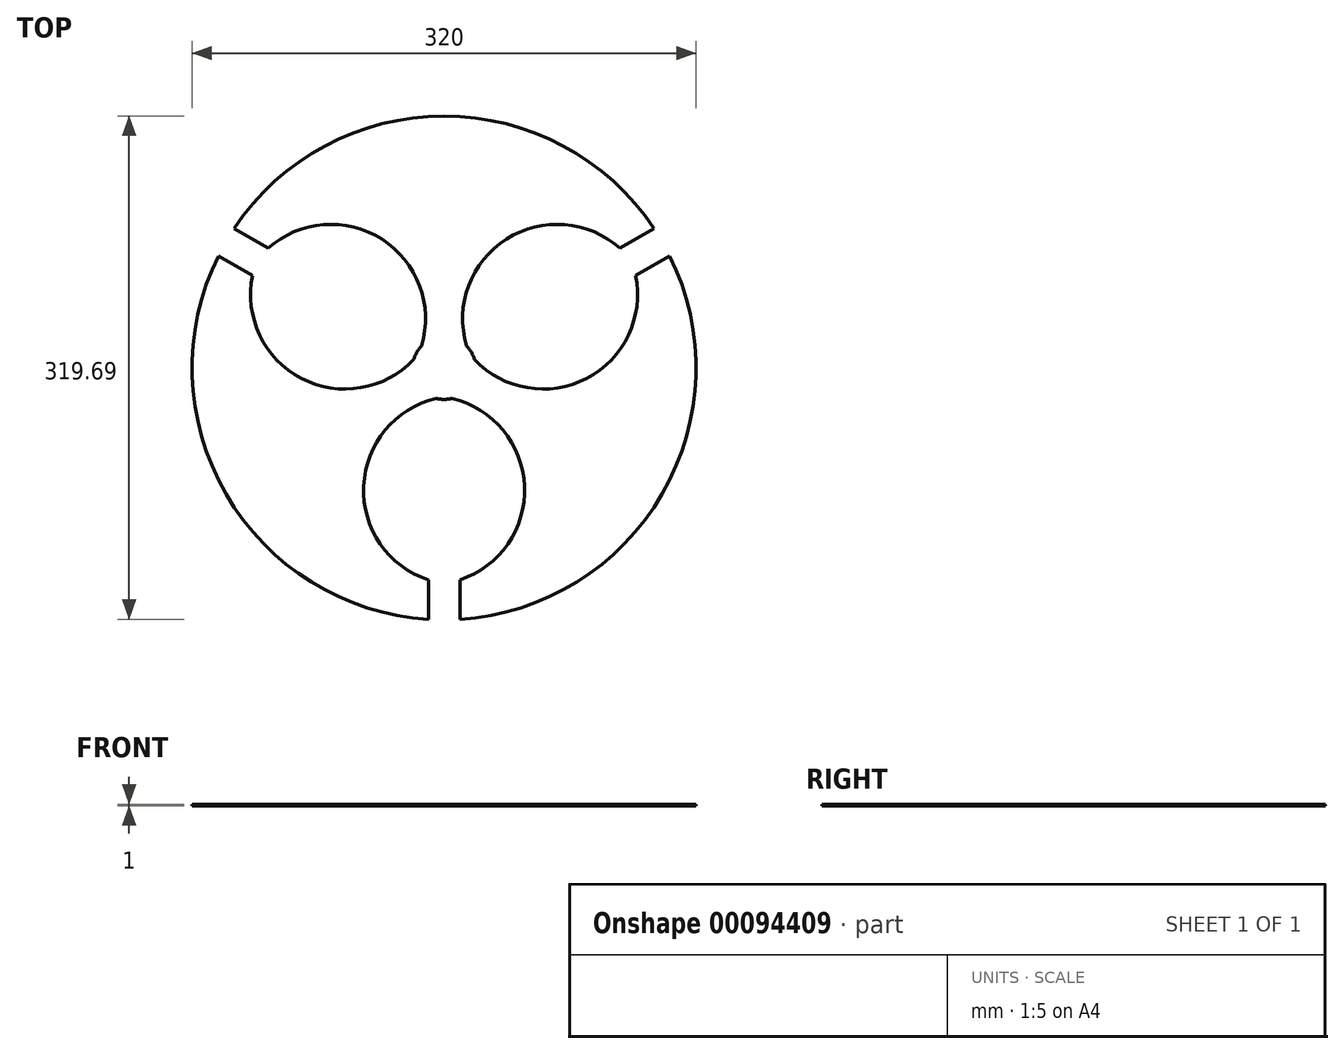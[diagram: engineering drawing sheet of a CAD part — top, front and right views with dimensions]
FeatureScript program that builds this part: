
annotation { "Feature Type Name" : "Feature", "Feature Type Description" : "" }
export const myFeature = defineFeature(function(context is Context, id is Id, definition is map)
    precondition{}
    {
        {
            var Q0;
            Q0=qCreatedBy(makeId("Top.planeOp"),FACE);
            var sketch = newSketch(context, id + "F0", { "sketchPlane" : qUnion([Q0])});
            skArc(sketch, "E0", {"start": v(-5, -19.36) * mm, "mid": v(0, -20) * mm, "end": v(5, -19.36) * mm});
            skArc(sketch, "E1", {"start": v(10, -159.69) * mm, "mid": v(138.56, -80) * mm, "end": v(143.3, 71.18) * mm});
            skLineSegment(sketch, "E2", {"start": v(0, 0) * mm, "end": v(0, -160) * mm, "construction": true});
            skLineSegment(sketch, "E3", {"start": v(0, 0) * mm, "end": v(-138.56, 80) * mm, "construction": true});
            skLineSegment(sketch, "E4", {"start": v(0, 0) * mm, "end": v(138.56, 80) * mm, "construction": true});
            skLineSegment(sketch, "E5", {"start": v(-10, -159.69) * mm, "end": v(-10, -134.69) * mm});
            skLineSegment(sketch, "E6", {"start": v(10, -159.69) * mm, "end": v(10, -134.69) * mm});
            skArc(sketch, "E7", {"start": v(-5, -19.36) * mm, "mid": v(-51.06, -75.14) * mm, "end": v(-10, -134.69) * mm});
            skArc(sketch, "E8", {"start": v(10, -134.69) * mm, "mid": v(51.06, -75.14) * mm, "end": v(5, -19.36) * mm});
            skArc(sketch, "E9.1.0", {"start": v(19.27, 5.35) * mm, "mid": v(90.6, -6.65) * mm, "end": v(121.64, 58.68) * mm});
            skLineSegment(sketch, "E9.1.1", {"start": v(133.3, 88.5) * mm, "end": v(111.64, 76) * mm});
            skLineSegment(sketch, "E9.1.2", {"start": v(143.3, 71.18) * mm, "end": v(121.64, 58.68) * mm});
            skArc(sketch, "E9.1.3", {"start": v(111.64, 76) * mm, "mid": v(39.54, 81.79) * mm, "end": v(14.27, 14.01) * mm});
            skArc(sketch, "E9.2.0", {"start": v(-14.27, 14.01) * mm, "mid": v(-39.54, 81.79) * mm, "end": v(-111.64, 76) * mm});
            skLineSegment(sketch, "E9.2.1", {"start": v(-143.3, 71.18) * mm, "end": v(-121.64, 58.68) * mm});
            skLineSegment(sketch, "E9.2.2", {"start": v(-133.3, 88.5) * mm, "end": v(-111.64, 76) * mm});
            skArc(sketch, "E9.2.3", {"start": v(-121.64, 58.68) * mm, "mid": v(-90.6, -6.65) * mm, "end": v(-19.27, 5.35) * mm});
            skArc(sketch, "E10.trimOffspring", {"start": v(-143.3, 71.18) * mm, "mid": v(-138.56, -80) * mm, "end": v(-10, -159.69) * mm});
            skArc(sketch, "E11.trimOffspring", {"start": v(133.3, 88.5) * mm, "mid": v(0, 160) * mm, "end": v(-133.3, 88.5) * mm});
            skArc(sketch, "E12.trimOffspring", {"start": v(-14.27, 14.01) * mm, "mid": v(-17.32, 10) * mm, "end": v(-19.27, 5.35) * mm});
            skArc(sketch, "E13.trimOffspring", {"start": v(19.27, 5.35) * mm, "mid": v(17.32, 10) * mm, "end": v(14.27, 14.01) * mm});
            skSolve(sketch);
        }
        {
            var Q0;
            Q0 = qSketchRegion(id + "F0", true);
            extrude(context, id + "F1", {"entities" : qUnion([Q0]), "depth" : 1 * mm});
        }
    });
